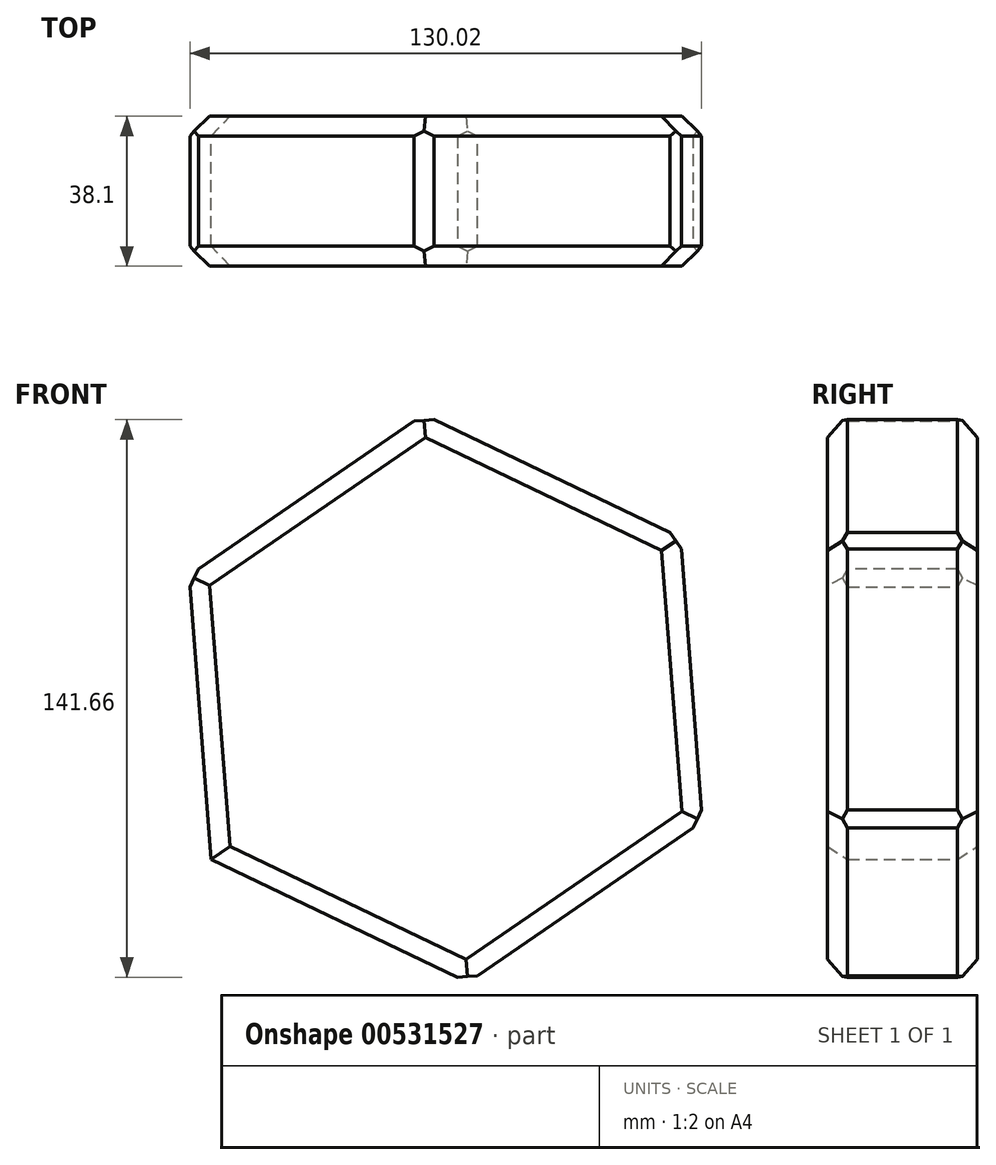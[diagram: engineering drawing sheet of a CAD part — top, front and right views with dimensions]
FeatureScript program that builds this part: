
annotation { "Feature Type Name" : "Feature", "Feature Type Description" : "" }
export const myFeature = defineFeature(function(context is Context, id is Id, definition is map)
    precondition{}
    {
        {
            var Q0;
            Q0=qCreatedBy(makeId("Front.planeOp"),FACE);
            var sketch = newSketch(context, id + "F0", { "sketchPlane" : qUnion([Q0])});
            skCircle(sketch, "E0.cCircle", {"center": v(0, 0) * mm, "radius": 62.63 * mm, "construction": true});
            skLineSegment(sketch, "E0.0", {"start": v(65.24, -31.2) * mm, "end": v(5.6, -72.1) * mm});
            skLineSegment(sketch, "E0.1", {"start": v(5.6, -72.1) * mm, "end": v(-59.64, -40.9) * mm});
            skLineSegment(sketch, "E0.2", {"start": v(-59.64, -40.9) * mm, "end": v(-65.24, 31.2) * mm});
            skLineSegment(sketch, "E0.3", {"start": v(-65.24, 31.2) * mm, "end": v(-5.6, 72.1) * mm});
            skLineSegment(sketch, "E0.4", {"start": v(-5.6, 72.1) * mm, "end": v(59.64, 40.9) * mm});
            skLineSegment(sketch, "E0.5", {"start": v(59.64, 40.9) * mm, "end": v(65.24, -31.2) * mm});
            skPoint(sketch, "E0.0.midPoint", {"position": v(35.42, -51.65) * mm});
            skSolve(sketch);
        }
        {
            var Q0;
            Q0=makeQuery(id+"F0.imprint","IMPRINT",FACE,{"disambiguationData":[TD([[makeQuery(id+"F0.imprint","IMPRINT",EDGE,{"derivedFrom":sQuery(id+"F0.wireOp",EDGE,"E0.0")}),-1.0]])]});
            extrude(context, id + "F1", {"entities" : qUnion([Q0]), "depth" : 38.1 * mm, "offsetDistance" : 25.4 * mm});
        }
        {
            var Q0;
            Q0=makeQuery(id+"F1.opExtrude","CAP_EDGE",EDGE,{"disambiguationData":[OSD([sQuery(id+"F0.wireOp",EDGE,"E0.4")])],"isStart":false});
            chamfer(context, id + "F2", {"entities" : qUnion([Q0]), "width" : 5.08 * mm, "tangentPropagation" : true});
        }
        {
            var Q0;
            Q0=makeQuery(id+"F1.opExtrude","CAP_EDGE",EDGE,{"disambiguationData":[OSD([sQuery(id+"F0.wireOp",EDGE,"E0.5")])],"isStart":false});
            chamfer(context, id + "F3", {"entities" : qUnion([Q0]), "width" : 5.08 * mm, "tangentPropagation" : true});
        }
        {
            var Q0;
            Q0=makeQuery(id+"F1.opExtrude","CAP_EDGE",EDGE,{"disambiguationData":[OSD([sQuery(id+"F0.wireOp",EDGE,"E0.2")])],"isStart":true});
            var Q1;
            Q1=makeQuery(id+"F1.opExtrude","CAP_EDGE",EDGE,{"disambiguationData":[OSD([sQuery(id+"F0.wireOp",EDGE,"E0.5")])],"isStart":true});
            var Q2;
            Q2=makeQuery(id+"F1.opExtrude","CAP_EDGE",EDGE,{"disambiguationData":[OSD([sQuery(id+"F0.wireOp",EDGE,"E0.1")])],"isStart":true});
            var Q3;
            Q3=makeQuery(id+"F1.opExtrude","CAP_EDGE",EDGE,{"disambiguationData":[OSD([sQuery(id+"F0.wireOp",EDGE,"E0.0")])],"isStart":false});
            var Q4;
            Q4=makeQuery(id+"F1.opExtrude","CAP_EDGE",EDGE,{"disambiguationData":[OSD([sQuery(id+"F0.wireOp",EDGE,"E0.3")])],"isStart":true});
            var Q5;
            Q5=makeQuery(id+"F1.opExtrude","CAP_EDGE",EDGE,{"disambiguationData":[OSD([sQuery(id+"F0.wireOp",EDGE,"E0.1")])],"isStart":false});
            var Q6;
            Q6=makeQuery(id+"F1.opExtrude","CAP_EDGE",EDGE,{"disambiguationData":[OSD([sQuery(id+"F0.wireOp",EDGE,"E0.4")])],"isStart":true});
            var Q7;
            Q7=makeQuery(id+"F1.opExtrude","CAP_EDGE",EDGE,{"disambiguationData":[OSD([sQuery(id+"F0.wireOp",EDGE,"E0.2")])],"isStart":false});
            var Q8;
            Q8=makeQuery(id+"F1.opExtrude","CAP_EDGE",EDGE,{"disambiguationData":[OSD([sQuery(id+"F0.wireOp",EDGE,"E0.0")])],"isStart":true});
            var Q9;
            Q9=makeQuery(id+"F1.opExtrude","CAP_EDGE",EDGE,{"disambiguationData":[OSD([sQuery(id+"F0.wireOp",EDGE,"E0.3")])],"isStart":false});
            chamfer(context, id + "F4", {"entities" : qUnion([Q0, Q1, Q2, Q3, Q4, Q5, Q6, Q7, Q8, Q9]), "width" : 5.08 * mm, "tangentPropagation" : true});
        }
        {
            var Q0;
            Q0=makeQuery(id+"F1.opExtrude","SWEPT_EDGE",EDGE,{"disambiguationData":[OSD([sQuery(id+"F0.wireOp",EDGE,"E0.0"),sQuery(id+"F0.wireOp",EDGE,"E0.1")])]});
            chamfer(context, id + "F5", {"entities" : qUnion([Q0]), "width" : 5.08 * mm, "tangentPropagation" : true});
        }
        {
            var Q0;
            Q0=makeQuery(id+"F1.opExtrude","SWEPT_EDGE",EDGE,{"disambiguationData":[OSD([sQuery(id+"F0.wireOp",EDGE,"E0.3"),sQuery(id+"F0.wireOp",EDGE,"E0.4")])]});
            var Q1;
            Q1=makeQuery(id+"F1.opExtrude","SWEPT_EDGE",EDGE,{"disambiguationData":[OSD([sQuery(id+"F0.wireOp",EDGE,"E0.2"),sQuery(id+"F0.wireOp",EDGE,"E0.3")])]});
            var Q2;
            Q2=makeQuery(id+"F1.opExtrude","SWEPT_EDGE",EDGE,{"disambiguationData":[OSD([sQuery(id+"F0.wireOp",EDGE,"E0.0"),sQuery(id+"F0.wireOp",EDGE,"E0.5")])]});
            var Q3;
            Q3=makeQuery(id+"F1.opExtrude","SWEPT_EDGE",EDGE,{"disambiguationData":[OSD([sQuery(id+"F0.wireOp",EDGE,"E0.4"),sQuery(id+"F0.wireOp",EDGE,"E0.5")])]});
            chamfer(context, id + "F6", {"entities" : qUnion([Q0, Q1, Q2, Q3]), "width" : 5.08 * mm, "tangentPropagation" : true});
        }
        {
            var Q0;
            Q0=makeQuery(id+"F1.opExtrude","CAP_FACE",FACE,{"disambiguationData":[OSD([sQuery(id+"F0.wireOp",EDGE,"E0.0"),sQuery(id+"F0.wireOp",EDGE,"E0.1"),sQuery(id+"F0.wireOp",EDGE,"E0.2"),sQuery(id+"F0.wireOp",EDGE,"E0.3"),sQuery(id+"F0.wireOp",EDGE,"E0.4"),sQuery(id+"F0.wireOp",EDGE,"E0.5")])],"isStart":false});
            var sketch = newSketch(context, id + "F7", { "sketchPlane" : qUnion([Q0])});
            skCircle(sketch, "E1", {"center": v(0, 0) * mm, "radius": 43.85 * mm});
            skSolve(sketch);
        }
        {
            var Q0;
            Q0=sQuery(id+"F7.wireOp",EDGE,"E1");
            extrude(context, id + "F8", {"bodyType" : ToolBodyType.SURFACE, "surfaceEntities" : qUnion([Q0]), "depth" : 63.5 * mm, "offsetDistance" : 25.4 * mm});
        }
    });
